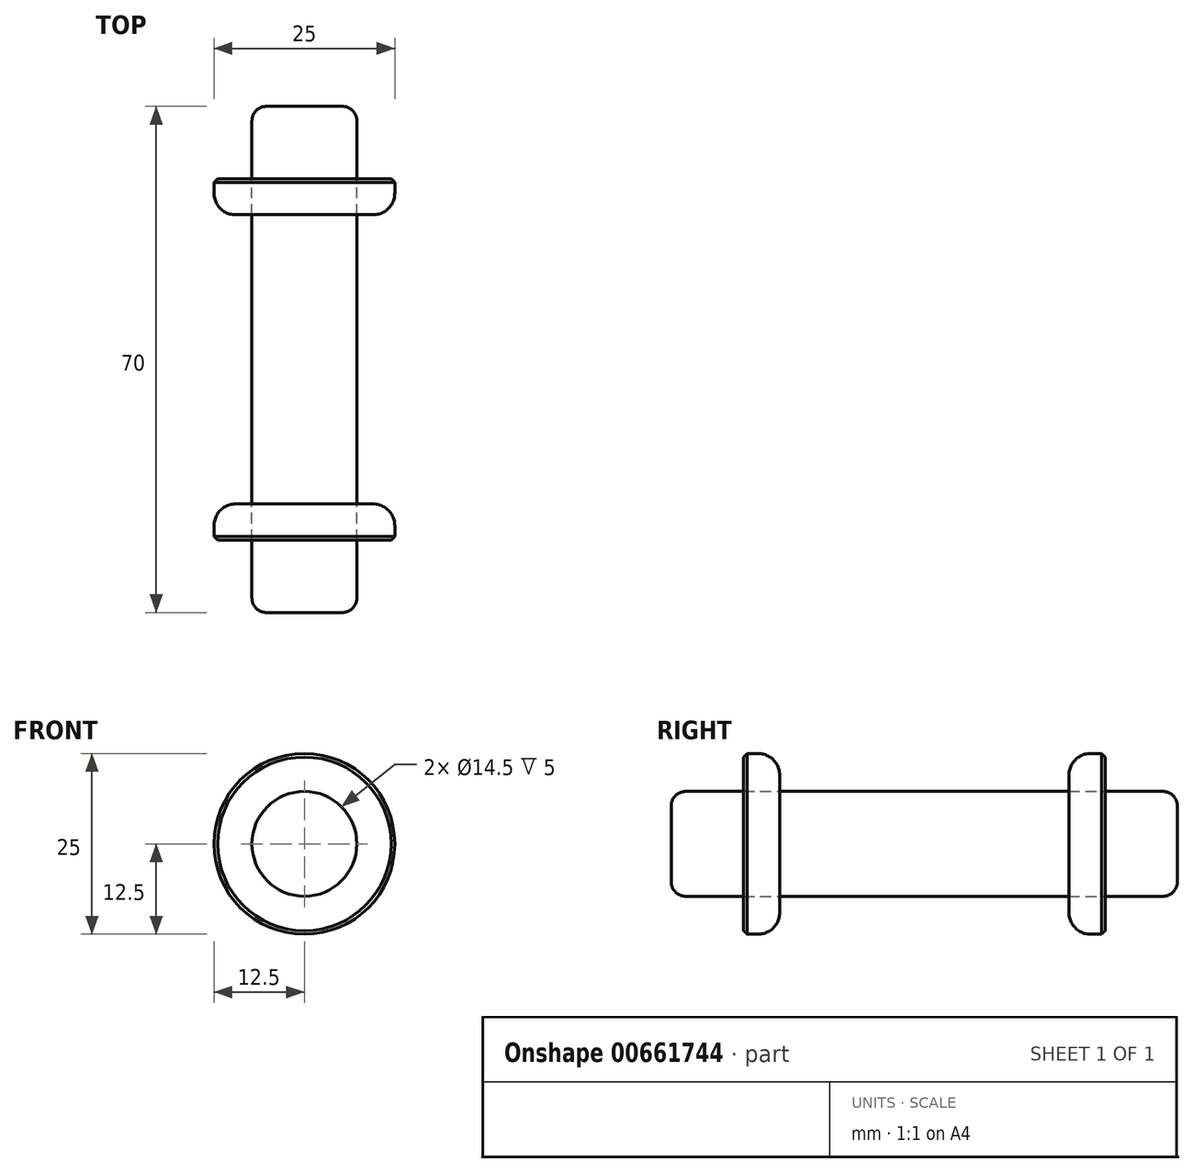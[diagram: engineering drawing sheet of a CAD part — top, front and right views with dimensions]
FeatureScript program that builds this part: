
annotation { "Feature Type Name" : "Feature", "Feature Type Description" : "" }
export const myFeature = defineFeature(function(context is Context, id is Id, definition is map)
    precondition{}
    {
        {
            var Q0;
            Q0=qCreatedBy(makeId("Front.planeOp"),FACE);
            var sketch = newSketch(context, id + "F0", { "sketchPlane" : qUnion([Q0])});
            skCircle(sketch, "E0", {"center": v(0, 0) * mm, "radius": 7.25 * mm});
            skCircle(sketch, "E1", {"center": v(0, 0) * mm, "radius": 12.5 * mm});
            skSolve(sketch);
        }
        {
            var Q0;
            Q0=makeQuery(id+"F0.imprint","IMPRINT",FACE,{"disambiguationData":[TD([[makeQuery(id+"F0.imprint","IMPRINT",EDGE,{"derivedFrom":sQuery(id+"F0.wireOp",EDGE,"E0")}),1.0]])]});
            extrude(context, id + "F1", {"entities" : qUnion([Q0]), "endBound" : BoundingType.SYMMETRIC, "depth" : 70 * mm, "offsetDistance" : 25 * mm});
        }
        {
            var Q0;
            Q0=makeQuery(id+"F1.opExtrude","CAP_EDGE",EDGE,{"disambiguationData":[OSD([sQuery(id+"F0.wireOp",EDGE,"E0")])],"isStart":false});
            var Q1;
            Q1=makeQuery(id+"F1.opExtrude","CAP_EDGE",EDGE,{"disambiguationData":[OSD([sQuery(id+"F0.wireOp",EDGE,"E0")])],"isStart":true});
            fillet(context, id + "F2", {"entities" : qUnion([Q0, Q1]), "radius" : 2 * mm, "tangentPropagation" : true, "allowEdgeOverflow" : false});
        }
        {
            var Q0;
            Q0=makeQuery(id+"F0.imprint","IMPRINT",FACE,{"disambiguationData":[TD([[makeQuery(id+"F0.imprint","IMPRINT",EDGE,{"derivedFrom":sQuery(id+"F0.wireOp",EDGE,"E0")}),-1.0]])]});
            extrude(context, id + "F3", {"entities" : qUnion([Q0]), "depth" : 5 * mm, "offsetDistance" : 25 * mm});
        }
        {
            var Q0;
            Q0=makeQuery(id+"F3.opExtrude","SWEPT_BODY",BODY,{"disambiguationData":[OSD([sQuery(id+"F0.wireOp",EDGE,"E0"),sQuery(id+"F0.wireOp",EDGE,"E1")])]});
            var Q1;
            Q1=makeQuery(id+"F1.opExtrude","SWEPT_FACE",FACE,{"disambiguationData":[OSD([sQuery(id+"F0.wireOp",EDGE,"E0")])]});
            transform(context, id + "F4", {"entities" : qUnion([Q0]), "transformType" : TransformType.TRANSLATION_DISTANCE, "transformDirection" : qUnion([Q1]), "distance" : 20 * mm, "oppositeDirection" : true, "makeCopy" : true});
        }
        {
            var Q0;
            Q0=makeQuery(id+"F3.opExtrude","SWEPT_BODY",BODY,{"disambiguationData":[OSD([sQuery(id+"F0.wireOp",EDGE,"E0"),sQuery(id+"F0.wireOp",EDGE,"E1")])]});
            var Q1;
            Q1=makeQuery(id+"F1.opExtrude","SWEPT_FACE",FACE,{"disambiguationData":[OSD([sQuery(id+"F0.wireOp",EDGE,"E0")])]});
            transform(context, id + "F5", {"entities" : qUnion([Q0]), "transformType" : TransformType.TRANSLATION_DISTANCE, "transformDirection" : qUnion([Q1]), "distance" : 25 * mm, "makeCopy" : false});
        }
        {
            var Q0;
            Q0=makeQuery(id+"F4.opPattern","COPY",EDGE,{"derivedFrom":makeQuery(id+"F3.opExtrude","CAP_EDGE",EDGE,{"disambiguationData":[OSD([sQuery(id+"F0.wireOp",EDGE,"E1")])],"isStart":true}),"instanceName":"1"});
            var Q1;
            Q1=makeQuery(id+"F3.opExtrude","CAP_EDGE",EDGE,{"disambiguationData":[OSD([sQuery(id+"F0.wireOp",EDGE,"E1")])],"isStart":false});
            fillet(context, id + "F6", {"entities" : qUnion([Q0, Q1]), "radius" : 3 * mm, "tangentPropagation" : true, "allowEdgeOverflow" : false});
        }
        {
            var Q0;
            Q0=makeQuery(id+"F4.opPattern","COPY",EDGE,{"derivedFrom":makeQuery(id+"F3.opExtrude","CAP_EDGE",EDGE,{"disambiguationData":[OSD([sQuery(id+"F0.wireOp",EDGE,"E1")])],"isStart":false}),"instanceName":"1"});
            var Q1;
            Q1=makeQuery(id+"F3.opExtrude","CAP_EDGE",EDGE,{"disambiguationData":[OSD([sQuery(id+"F0.wireOp",EDGE,"E1")])],"isStart":true});
            chamfer(context, id + "F7", {"entities" : qUnion([Q0, Q1]), "width" : 0.5 * mm, "tangentPropagation" : true});
        }
    });
